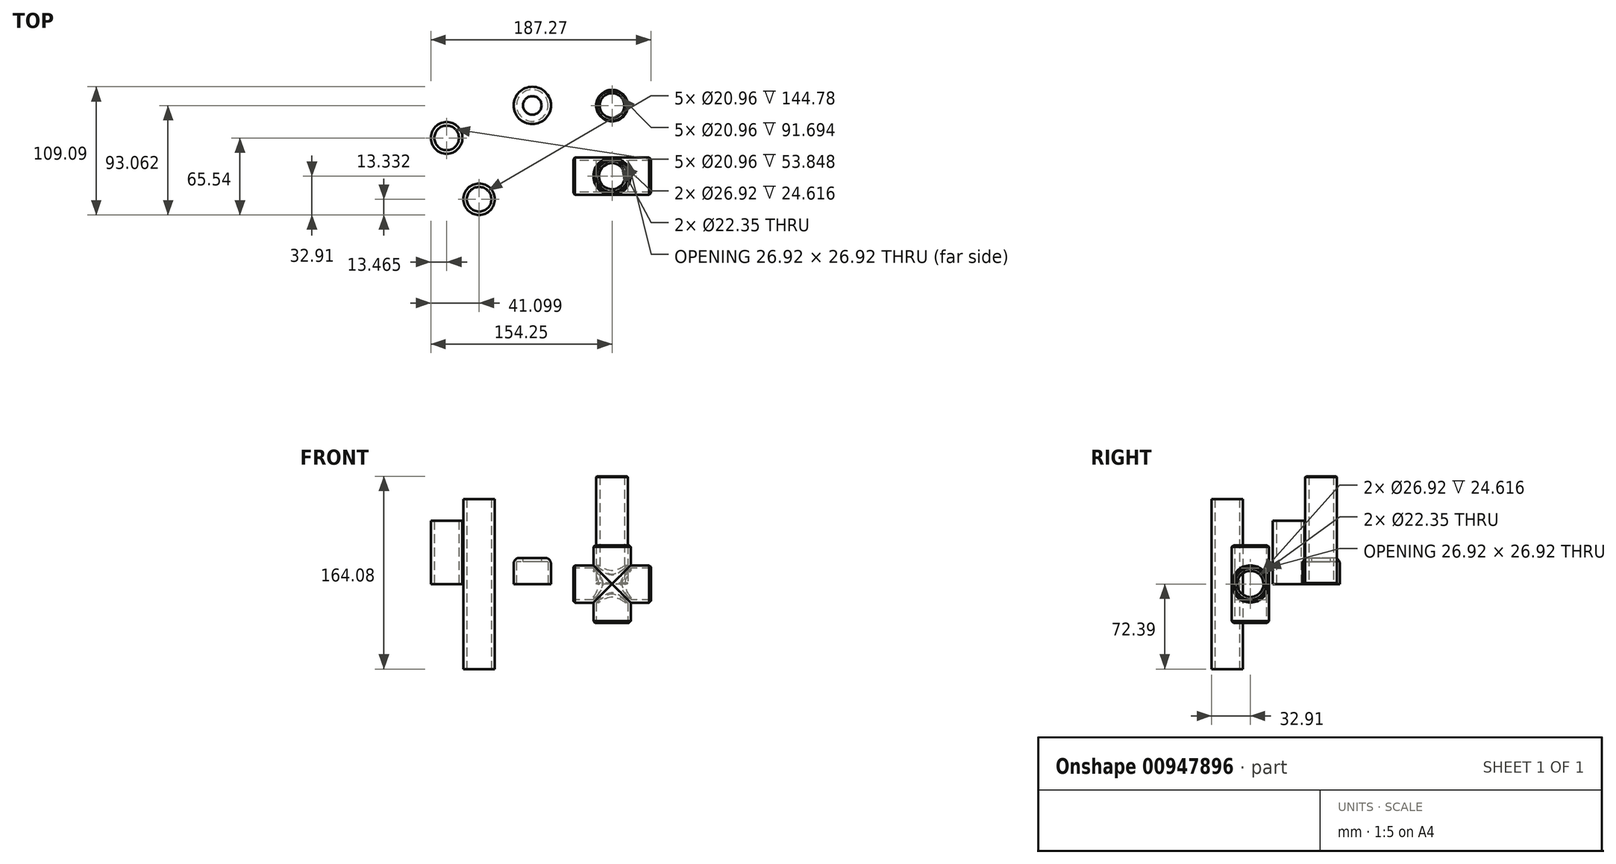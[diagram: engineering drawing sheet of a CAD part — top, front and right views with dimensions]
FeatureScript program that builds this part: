
annotation { "Feature Type Name" : "Feature", "Feature Type Description" : "" }
export const myFeature = defineFeature(function(context is Context, id is Id, definition is map)
    precondition{}
    {
        {
            var Q0;
            Q0=qCreatedBy(makeId("Top.planeOp"),FACE);
            var sketch = newSketch(context, id + "F0", { "sketchPlane" : qUnion([Q0])});
            skCircle(sketch, "E0", {"center": v(0, 0) * mm, "radius": 13.46 * mm});
            skCircle(sketch, "E1", {"center": v(0, 0) * mm, "radius": 15.88 * mm});
            skSolve(sketch);
        }
        {
            var Q0;
            Q0 = qSketchRegion(id + "F0", true);
            extrude(context, id + "F1", {"entities" : qUnion([Q0]), "endBound" : BoundingType.SYMMETRIC, "depth" : 66.04 * mm, "offsetDistance" : 25.4 * mm});
        }
        {
            var Q0;
            Q0=qCreatedBy(makeId("Right.planeOp"),FACE);
            var sketch = newSketch(context, id + "F2", { "sketchPlane" : qUnion([Q0])});
            skCircle(sketch, "E2", {"center": v(0, 0) * mm, "radius": 15.88 * mm});
            skCircle(sketch, "E3", {"center": v(0, 0) * mm, "radius": 13.46 * mm});
            skSolve(sketch);
        }
        {
            var Q0;
            Q0 = qSketchRegion(id + "F2", true);
            extrude(context, id + "F3", {"entities" : qUnion([Q0]), "operationType" : NewBodyOperationType.ADD, "endBound" : BoundingType.SYMMETRIC, "depth" : 66.04 * mm, "offsetDistance" : 25.4 * mm});
        }
        {
            var Q0;
            Q0=makeQuery(id+"F1.opExtrude","CAP_FACE",FACE,{"disambiguationData":[OSD([sQuery(id+"F0.wireOp",EDGE,"E0"),sQuery(id+"F0.wireOp",EDGE,"E1")])],"isStart":false});
            var sketch = newSketch(context, id + "F4", { "sketchPlane" : qUnion([Q0])});
            skCircle(sketch, "E4", {"center": v(0, 0) * mm, "radius": 11.18 * mm});
            skSolve(sketch);
        }
        {
            var Q0;
            Q0 = qSketchRegion(id + "F4", true);
            extrude(context, id + "F5", {"entities" : qUnion([Q0]), "operationType" : NewBodyOperationType.REMOVE, "oppositeDirection" : true, "depth" : 76.2 * mm, "offsetDistance" : 25.4 * mm});
        }
        {
            var Q0;
            Q0=makeQuery(id+"F3.opExtrude","CAP_FACE",FACE,{"disambiguationData":[OSD([sQuery(id+"F2.wireOp",EDGE,"E2"),sQuery(id+"F2.wireOp",EDGE,"E3")])],"isStart":false});
            var sketch = newSketch(context, id + "F6", { "sketchPlane" : qUnion([Q0])});
            skCircle(sketch, "E5", {"center": v(0, 0) * mm, "radius": 11.18 * mm});
            skSolve(sketch);
        }
        {
            var Q0;
            Q0 = qSketchRegion(id + "F6", true);
            extrude(context, id + "F7", {"entities" : qUnion([Q0]), "operationType" : NewBodyOperationType.REMOVE, "oppositeDirection" : true, "depth" : 76.2 * mm, "offsetDistance" : 25.4 * mm});
        }
        {
            var Q0;
            Q0=makeQuery(id+"F1.opExtrude","CAP_EDGE",EDGE,{"disambiguationData":[OSD([sQuery(id+"F0.wireOp",EDGE,"E1")])],"isStart":false});
            var Q1;
            Q1=makeQuery(id+"F3.opExtrude","CAP_EDGE",EDGE,{"disambiguationData":[OSD([sQuery(id+"F2.wireOp",EDGE,"E2")])],"isStart":false});
            var Q2;
            Q2=makeQuery(id+"F1.opExtrude","CAP_EDGE",EDGE,{"disambiguationData":[OSD([sQuery(id+"F0.wireOp",EDGE,"E1")])],"isStart":true});
            var Q3;
            Q3=makeQuery(id+"F3.opExtrude","CAP_EDGE",EDGE,{"disambiguationData":[OSD([sQuery(id+"F2.wireOp",EDGE,"E2")])],"isStart":true});
            chamfer(context, id + "F8", {"entities" : qUnion([Q0, Q1, Q2, Q3]), "width" : 1.52 * mm, "tangentPropagation" : true});
        }
        {
            var Q0;
            Q0=qCreatedBy(makeId("Top.planeOp"),FACE);
            var sketch = newSketch(context, id + "F9", { "sketchPlane" : qUnion([Q0])});
            skCircle(sketch, "E6", {"center": v(0, 60.15) * mm, "radius": 10.48 * mm});
            skCircle(sketch, "E7", {"center": v(0, 60.15) * mm, "radius": 13.46 * mm});
            skSolve(sketch);
        }
        {
            var Q0;
            Q0 = qSketchRegion(id + "F9", true);
            extrude(context, id + "F10", {"entities" : qUnion([Q0]), "depth" : 91.7 * mm, "offsetDistance" : 25.4 * mm});
        }
        {
            var Q0;
            Q0=makeQuery(id+"F10.opExtrude","CAP_EDGE",EDGE,{"disambiguationData":[OSD([sQuery(id+"F9.wireOp",EDGE,"E7")])],"isStart":true});
            var Q1;
            Q1=makeQuery(id+"F10.opExtrude","CAP_EDGE",EDGE,{"disambiguationData":[OSD([sQuery(id+"F9.wireOp",EDGE,"E7")])],"isStart":false});
            chamfer(context, id + "F11", {"entities" : qUnion([Q0, Q1]), "width" : 0.76 * mm, "tangentPropagation" : true});
        }
        {
            var Q0;
            Q0=qCreatedBy(makeId("Top.planeOp"),FACE);
            var sketch = newSketch(context, id + "F12", { "sketchPlane" : qUnion([Q0])});
            skCircle(sketch, "E8", {"center": v(-67.87, 60.3) * mm, "radius": 13.46 * mm});
            skCircle(sketch, "E9", {"center": v(-67.87, 60.3) * mm, "radius": 15.88 * mm});
            skSolve(sketch);
        }
        {
            var Q0;
            Q0 = qSketchRegion(id + "F12", true);
            extrude(context, id + "F13", {"entities" : qUnion([Q0]), "depth" : 19.05 * mm, "offsetDistance" : 25.4 * mm});
        }
        {
            var Q0;
            Q0=makeQuery(id+"F13.opExtrude","CAP_FACE",FACE,{"disambiguationData":[OSD([sQuery(id+"F12.wireOp",EDGE,"E8"),sQuery(id+"F12.wireOp",EDGE,"E9")])],"isStart":false});
            var sketch = newSketch(context, id + "F14", { "sketchPlane" : qUnion([Q0])});
            skCircle(sketch, "E10", {"center": v(-67.87, 60.3) * mm, "radius": 15.88 * mm});
            skSolve(sketch);
        }
        {
            var Q0;
            Q0 = qSketchRegion(id + "F14", true);
            extrude(context, id + "F15", {"entities" : qUnion([Q0]), "operationType" : NewBodyOperationType.ADD, "depth" : 3.17 * mm, "offsetDistance" : 25.4 * mm});
        }
        {
            var Q0;
            Q0=makeQuery(id+"F15.opExtrude","CAP_FACE",FACE,{"disambiguationData":[OSD([sQuery(id+"F14.wireOp",EDGE,"E10")])],"isStart":false});
            fillet(context, id + "F16", {"entities" : qUnion([Q0]), "radius" : 5.08 * mm, "tangentPropagation" : true, "allowEdgeOverflow" : false});
        }
        {
            var Q0;
            Q0=makeQuery(id+"F15.opExtrude","CAP_FACE",FACE,{"disambiguationData":[OSD([sQuery(id+"F14.wireOp",EDGE,"E10")])],"isStart":false});
            var sketch = newSketch(context, id + "F17", { "sketchPlane" : qUnion([Q0])});
            skCircle(sketch, "E11", {"center": v(-67.87, 60.3) * mm, "radius": 7.87 * mm});
            skSolve(sketch);
        }
        {
            var Q0;
            Q0 = qSketchRegion(id + "F17", true);
            extrude(context, id + "F18", {"entities" : qUnion([Q0]), "operationType" : NewBodyOperationType.REMOVE, "oppositeDirection" : true, "depth" : 25.4 * mm, "offsetDistance" : 25.4 * mm});
        }
        {
            var Q0;
            Q0=qCreatedBy(makeId("Top.planeOp"),FACE);
            var sketch = newSketch(context, id + "F19", { "sketchPlane" : qUnion([Q0])});
            skCircle(sketch, "E12", {"center": v(-113.15, -19.58) * mm, "radius": 13.34 * mm});
            skCircle(sketch, "E13", {"center": v(-113.15, -19.58) * mm, "radius": 10.48 * mm});
            skSolve(sketch);
        }
        {
            var Q0;
            Q0 = qSketchRegion(id + "F19", true);
            extrude(context, id + "F20", {"entities" : qUnion([Q0]), "endBound" : BoundingType.SYMMETRIC, "depth" : 144.78 * mm, "offsetDistance" : 25.4 * mm});
        }
        {
            var Q0;
            Q0=qCreatedBy(makeId("Top.planeOp"),FACE);
            var sketch = newSketch(context, id + "F21", { "sketchPlane" : qUnion([Q0])});
            skCircle(sketch, "E14", {"center": v(-140.79, 32.63) * mm, "radius": 13.46 * mm});
            skCircle(sketch, "E15", {"center": v(-140.79, 32.63) * mm, "radius": 10.48 * mm});
            skSolve(sketch);
        }
        {
            var Q0;
            Q0 = qSketchRegion(id + "F21", true);
            extrude(context, id + "F22", {"entities" : qUnion([Q0]), "depth" : 53.85 * mm, "offsetDistance" : 25.4 * mm});
        }
    });
